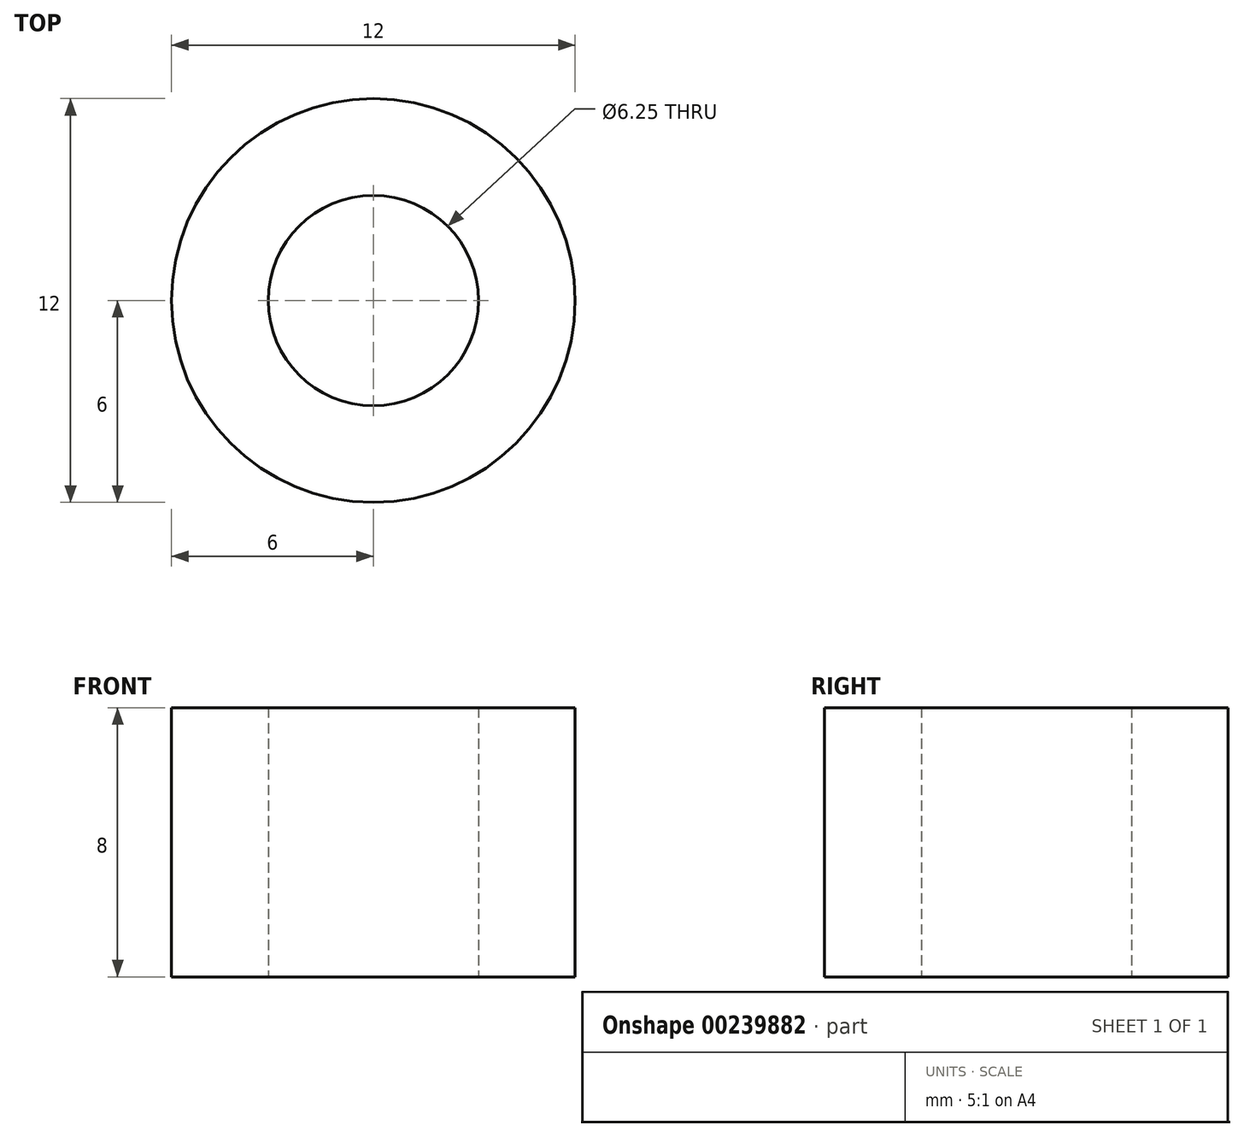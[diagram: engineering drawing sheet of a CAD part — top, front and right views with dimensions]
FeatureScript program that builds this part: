
annotation { "Feature Type Name" : "Feature", "Feature Type Description" : "" }
export const myFeature = defineFeature(function(context is Context, id is Id, definition is map)
    precondition{}
    {
        {
            var Q0;
            Q0=qCreatedBy(makeId("Top.planeOp"),FACE);
            var sketch = newSketch(context, id + "F0", { "sketchPlane" : qUnion([Q0])});
            skCircle(sketch, "E0", {"center": v(0, 0) * mm, "radius": 3.12 * mm});
            skCircle(sketch, "E1", {"center": v(0, 0) * mm, "radius": 6 * mm});
            skSolve(sketch);
        }
        {
            var Q0;
            Q0=makeQuery(id+"F0.imprint","IMPRINT",FACE,{"disambiguationData":[TD([[makeQuery(id+"F0.imprint","IMPRINT",EDGE,{"derivedFrom":sQuery(id+"F0.wireOp",EDGE,"E0")}),-1.0]])]});
            extrude(context, id + "F1", {"entities" : qUnion([Q0]), "depth" : 8 * mm});
        }
    });
